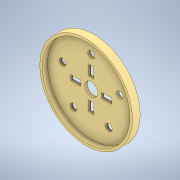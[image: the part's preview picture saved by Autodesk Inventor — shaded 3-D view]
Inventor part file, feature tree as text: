
AUTODESK INVENTOR PART (.ipt)
format: ipt  version: 2020.1 (Build 241239000, 239)  size: 267,264 bytes
history: native  units: in
note: dims shown in document units (in); Inventor stores cm internally (conversion verified against a paired STEP export)
features: sketch x5, extrude x3, hole x2, pattern_circular x2, projected_geometry x2, other x1, fillet x1
ambient origin geometry x8: Origin, YZ Plane, XZ Plane, XY Plane, X Axis, Y Axis, Z Axis, Center Point
bodies: Solid1 (feature_tree)
feature tree (16):
  parser-record x1  (decoder bookkeeping rows leaked as tree rows — omitted from the tree; the rows remain in map.json)
  extrude  "Extrusion1"  Depth=0.0787in
  extrude  "Extrusion2"  Depth=0.0787in
  hole  "Hole1"  [1 undecoded]
  hole  "Hole2"  [1 undecoded]
  pattern_circular  "Circular Pattern1"  [2 undecoded]
  extrude  "Extrusion5"  Depth=0.0098in
  fillet  "Fillet2"  [1 undecoded]
  pattern_circular  "Circular Pattern3"  [2 undecoded]
  sketch  "Sketch1"  dims[d0=2.8346in d1=0.0787in]
  sketch  "Sketch2"  dims[d2=0.0in d3=0.0787in]
  projected_geometry  "Projected Loop1"
  sketch  "Sketch4"  dims[d4=0.1575in d5=0.0in]
  sketch  "Sketch5"  dims[d6=0.3976in]
  sketch  "Sketch8"  dims[d7=0.75in d8=0.375in d9=0.25in d10=0.5635in d11=1.0in d12=0.8108in d13=0.9186in d14=0.2087in d15=0.75in d16=0.375in d17=0.25in d18=0.5635in d19=1.0in d20=0.8108in d21=1.9685in d22=360.0deg d43=0.1575in d44=0.315in d45=0.315in d46=1.0in d47=0.0137in d48=0.0787in d52=0.0098in d53=1.5748in d54=360.0deg d23=0.0625in d24=0.75in d25=0.375in]
  projected_geometry  "Projected Loop2"
note: 7 required parameter values undecoded (feature->parameter linkage not recoverable at this tier; creation-order binding heuristic only, values carry confidence <= 0.55)
note: 1 file-system path scrubbed to <path> (originals preserved in map.json)
